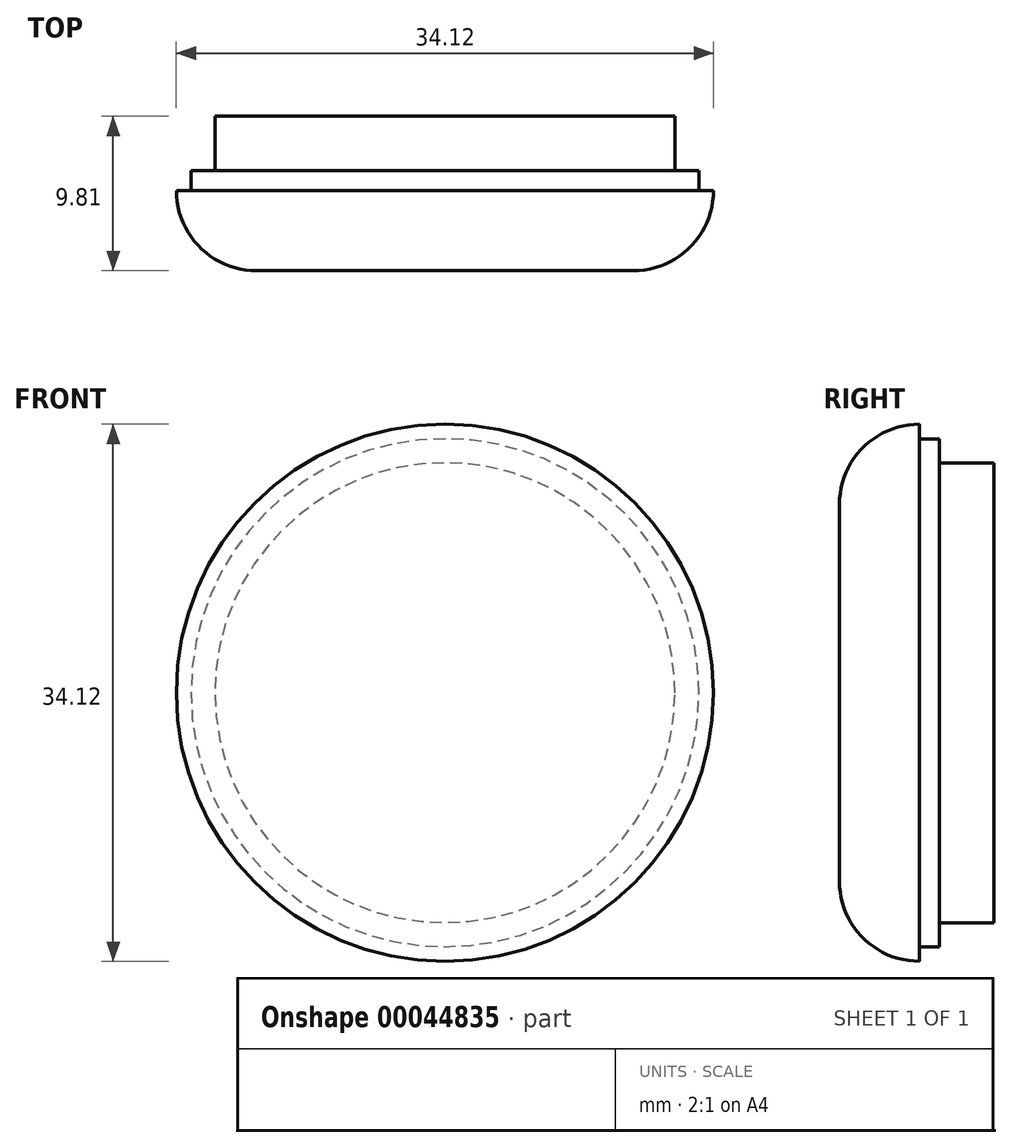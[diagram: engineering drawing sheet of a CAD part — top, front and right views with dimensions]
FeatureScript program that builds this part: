
annotation { "Feature Type Name" : "Feature", "Feature Type Description" : "" }
export const myFeature = defineFeature(function(context is Context, id is Id, definition is map)
    precondition{}
    {
        {
            var Q0;
            Q0=qCreatedBy(makeId("Front.planeOp"),FACE);
            var sketch = newSketch(context, id + "F0", { "sketchPlane" : qUnion([Q0])});
            skCircle(sketch, "E0", {"center": v(0, 0) * mm, "radius": 17.06 * mm});
            skSolve(sketch);
        }
        {
            var Q0;
            Q0=makeQuery(id+"F0.imprint","IMPRINT",FACE,{"disambiguationData":[TD([[makeQuery(id+"F0.imprint","IMPRINT",EDGE,{"derivedFrom":sQuery(id+"F0.wireOp",EDGE,"E0")}),1.0]])]});
            extrude(context, id + "F1", {"entities" : qUnion([Q0]), "oppositeDirection" : true, "depth" : 5.08 * mm});
        }
        {
            var Q0;
            Q0=makeQuery(id+"F1.opExtrude","CAP_FACE",FACE,{"disambiguationData":[OSD([sQuery(id+"F0.wireOp",EDGE,"E0")])],"isStart":false});
            var sketch = newSketch(context, id + "F2", { "sketchPlane" : qUnion([Q0])});
            skCircle(sketch, "E1", {"center": v(0, 0) * mm, "radius": 16.13 * mm});
            skSolve(sketch);
        }
        {
            var Q0;
            Q0=makeQuery(id+"F2.imprint","IMPRINT",FACE,{"disambiguationData":[TD([[makeQuery(id+"F2.imprint","IMPRINT",EDGE,{"derivedFrom":sQuery(id+"F2.wireOp",EDGE,"E1")}),1.0]])]});
            extrude(context, id + "F3", {"entities" : qUnion([Q0]), "operationType" : NewBodyOperationType.ADD, "depth" : 1.27 * mm});
        }
        {
            var Q0;
            Q0=makeQuery(id+"F1.opExtrude","CAP_EDGE",EDGE,{"disambiguationData":[OSD([sQuery(id+"F0.wireOp",EDGE,"E0")])],"isStart":true});
            fillet(context, id + "F4", {"entities" : qUnion([Q0]), "radius" : 5.08 * mm, "tangentPropagation" : true, "allowEdgeOverflow" : false});
        }
        {
            var Q0;
            Q0=makeQuery(id+"F3.opExtrude","CAP_FACE",FACE,{"disambiguationData":[OSD([sQuery(id+"F2.wireOp",EDGE,"E1")])],"isStart":false});
            var sketch = newSketch(context, id + "F5", { "sketchPlane" : qUnion([Q0])});
            skCircle(sketch, "E2", {"center": v(0, 0) * mm, "radius": 14.6 * mm});
            skSolve(sketch);
        }
        {
            var Q0;
            Q0=makeQuery(id+"F5.imprint","IMPRINT",FACE,{"disambiguationData":[TD([[makeQuery(id+"F5.imprint","IMPRINT",EDGE,{"derivedFrom":sQuery(id+"F5.wireOp",EDGE,"E2")}),1.0]])]});
            extrude(context, id + "F6", {"entities" : qUnion([Q0]), "operationType" : NewBodyOperationType.ADD, "depth" : 3.46 * mm});
        }
    });
